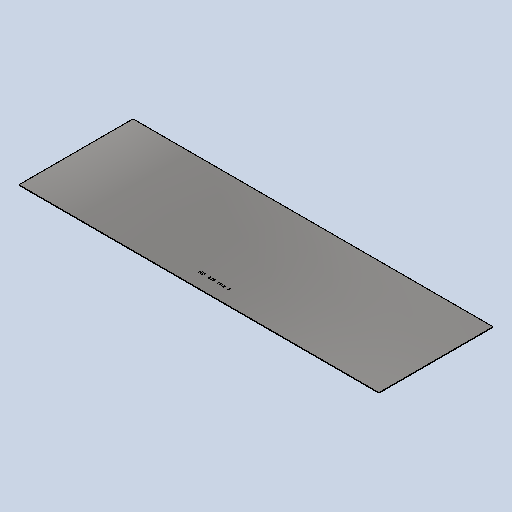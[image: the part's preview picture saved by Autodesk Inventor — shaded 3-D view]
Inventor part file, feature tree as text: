
AUTODESK INVENTOR PART (.ipt)
format: ipt  version: 2025 (Build 290162010, 162A)  size: 134,656 bytes
history: native  units: mm
features: other x2, sketch x2, sheet_metal_op x1
ambient origin geometry x8: Origin, YZ Plane, XZ Plane, XY Plane, X Axis, Y Axis, Z Axis, Center Point
bodies: Solid1 (feature_tree)
feature tree (5):
  sheet_metal_op  "Face1"
  other  "Mark1"
  sketch  "Sketch1"  dims[d0=1344.0mm]
  other  "Plate1"
  sketch  "Sketch2"  dims[d1=426.0mm d2=2.0mm d3=12.0mm d4=110.0mm d5=50.0mm]
